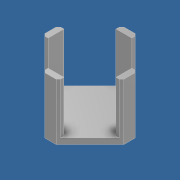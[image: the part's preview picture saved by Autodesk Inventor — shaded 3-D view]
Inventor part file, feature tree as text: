
AUTODESK INVENTOR PART (.ipt)
format: ipt  version: 2020 (Build 240168000, 168)  size: 2,246,144 bytes
history: mixed  units: mm
features: extrude x3, sketch x3, hole x2, pattern_circular x1, chamfer x1, fillet x1, imported_body x1
ambient origin geometry x8: Origin, YZ Plane, XZ Plane, XY Plane, X Axis, Y Axis, Z Axis, Center Point
bodies: Solid1 (imported_parasolid)
feature tree (12):
  extrude  "Extrusion1"  Depth=6.5mm TaperAngle=0.0deg
  hole  "Hole1"  [1 undecoded]
  hole  "Hole2"  [1 undecoded]
  extrude  "Extrusion3"  Depth=5.0mm TaperAngle=0.0deg
  extrude  "Extrusion4"  Depth=14.0mm
  pattern_circular  "Circular Pattern1"  [2 undecoded]
  chamfer  "Chamfer1"  Distance=30.0mm
  sketch  "Sketch1"  dims[d0=35.0mm d1=6.5mm d2=0.0mm]
  sketch  "Sketch4"  dims[d21=10.0mm d22=10.0mm d5=15.0mm d6=6.0mm d7=4.0mm d8=2.0mm d9=90.0deg d10=11.35mm d11=20.594885mm]
  sketch  "Sketch5"  dims[d29=10.0mm d30=10.0mm d14=15.0mm d15=6.0mm d16=4.0mm d17=2.0mm d18=90.0deg d19=21.4mm d20=20.594885mm d42=70.0mm d43=70.0mm d44=5.0mm d45=0.0mm d46=14.0mm d47=5.0mm d48=30.0mm d49=7.0mm d50=45.0mm d51=0.0mm d52=40.0mm d53=360.0deg d55=30.0mm d56=2.0mm d57=45.0deg]
  fillet  "Redondeo2"  Radius=7.0mm
  imported_body  NMx_Import_Brep_tag  [imported B-rep: ~995 faces, bbox_mm=[70.0, 56.5, 70.0]]
note: 4 required parameter values undecoded (feature->parameter linkage not recoverable at this tier; creation-order binding heuristic only, values carry confidence <= 0.55)
